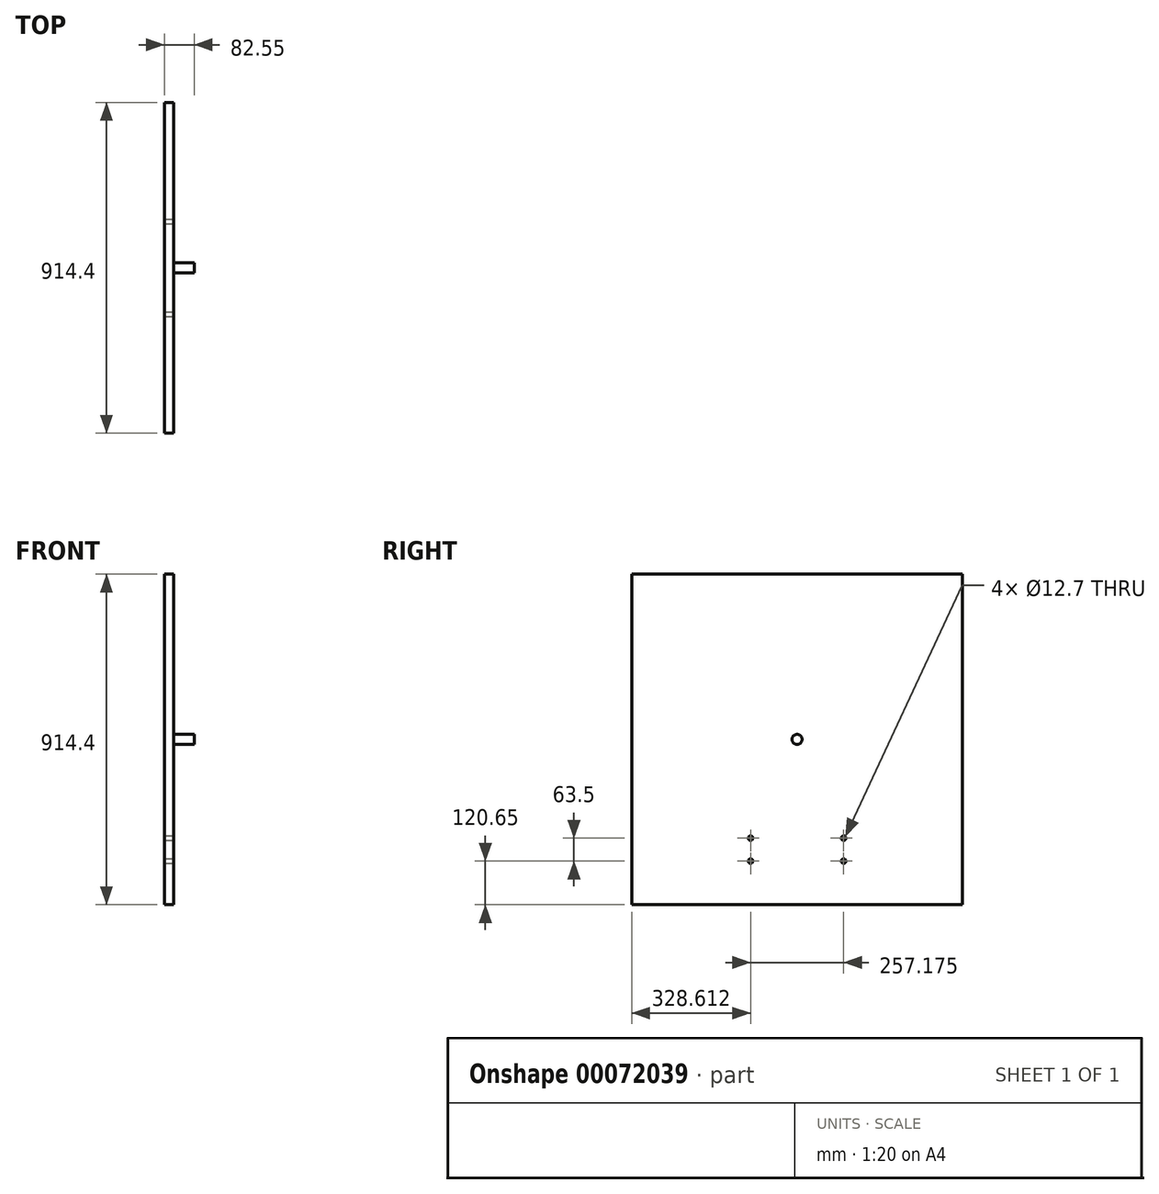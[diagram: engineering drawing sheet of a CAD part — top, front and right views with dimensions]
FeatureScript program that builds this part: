
annotation { "Feature Type Name" : "Feature", "Feature Type Description" : "" }
export const myFeature = defineFeature(function(context is Context, id is Id, definition is map)
    precondition{}
    {
        {
            var Q0;
            Q0=qCreatedBy(makeId("Right.planeOp"),FACE);
            var sketch = newSketch(context, id + "F0", { "sketchPlane" : qUnion([Q0])});
            skLineSegment(sketch, "E0.bottom", {"start": v(457.2, 457.2) * mm, "end": v(-457.2, 457.2) * mm});
            skLineSegment(sketch, "E0.top", {"start": v(457.2, -457.2) * mm, "end": v(-457.2, -457.2) * mm});
            skLineSegment(sketch, "E0.left", {"start": v(457.2, 457.2) * mm, "end": v(457.2, -457.2) * mm});
            skLineSegment(sketch, "E0.right", {"start": v(-457.2, 457.2) * mm, "end": v(-457.2, -457.2) * mm});
            skPoint(sketch, "E0.middle", {"position": v(0, 0) * mm});
            skSolve(sketch);
        }
        {
            var Q0;
            Q0=qSketchRegion(id+"F0",true);
            extrude(context, id + "F1", {"entities" : qUnion([Q0]), "depth" : 25.4 * mm});
        }
        {
            var Q0;
            Q0=makeQuery(id+"F1.opExtrude","CAP_FACE",FACE,{"disambiguationData":[OSD([sQuery(id+"F0.wireOp",EDGE,"E0.bottom"),sQuery(id+"F0.wireOp",EDGE,"E0.top"),sQuery(id+"F0.wireOp",EDGE,"E0.left"),sQuery(id+"F0.wireOp",EDGE,"E0.right")])],"isStart":false});
            var sketch = newSketch(context, id + "F2", { "sketchPlane" : qUnion([Q0])});
            skCircle(sketch, "E1", {"center": v(0, 0) * mm, "radius": 13.97 * mm});
            skSolve(sketch);
        }
        {
            var Q0;
            Q0=qSketchRegion(id+"F2",true);
            extrude(context, id + "F3", {"entities" : qUnion([Q0]), "operationType" : NewBodyOperationType.ADD, "depth" : 57.15 * mm});
        }
        {
            var Q0;
            Q0=makeQuery(id+"F1.opExtrude","CAP_FACE",FACE,{"disambiguationData":[OSD([sQuery(id+"F0.wireOp",EDGE,"E0.bottom"),sQuery(id+"F0.wireOp",EDGE,"E0.top"),sQuery(id+"F0.wireOp",EDGE,"E0.left"),sQuery(id+"F0.wireOp",EDGE,"E0.right")])],"isStart":false});
            var sketch = newSketch(context, id + "F4", { "sketchPlane" : qUnion([Q0])});
            skLineSegment(sketch, "E2.bottom", {"start": v(-128.59, -336.55) * mm, "end": v(128.59, -336.55) * mm});
            skLineSegment(sketch, "E2.top", {"start": v(-128.59, -273.05) * mm, "end": v(128.59, -273.05) * mm});
            skLineSegment(sketch, "E2.left", {"start": v(-128.59, -336.55) * mm, "end": v(-128.59, -273.05) * mm});
            skLineSegment(sketch, "E2.right", {"start": v(128.59, -336.55) * mm, "end": v(128.59, -273.05) * mm});
            skSolve(sketch);
        }
        {
            var Q0;
            Q0=sQuery(id+"F4.wireOp",VERTEX,"E2.left.end");
            var Q1;
            Q1=sQuery(id+"F4.wireOp",VERTEX,"E2.top.end");
            var Q2;
            Q2=sQuery(id+"F4.wireOp",VERTEX,"E2.right.start");
            var Q3;
            Q3=sQuery(id+"F4.wireOp",VERTEX,"E2.left.start");
            var Q4;
            Q4=makeQuery(id+"F1.opExtrude","SWEPT_BODY",BODY,{"disambiguationData":[OSD([sQuery(id+"F0.wireOp",EDGE,"E0.bottom"),sQuery(id+"F0.wireOp",EDGE,"E0.top"),sQuery(id+"F0.wireOp",EDGE,"E0.left"),sQuery(id+"F0.wireOp",EDGE,"E0.right")])]});
            hole(context, id + "F5", {"style" : HoleStyle.SIMPLE, "holeDiameter" : 12.7 * mm, "endStyle" : HoleEndStyle.THROUGH, "locations" : qUnion([Q0, Q1, Q2, Q3]), "scope" : qUnion([Q4])});
        }
    });
